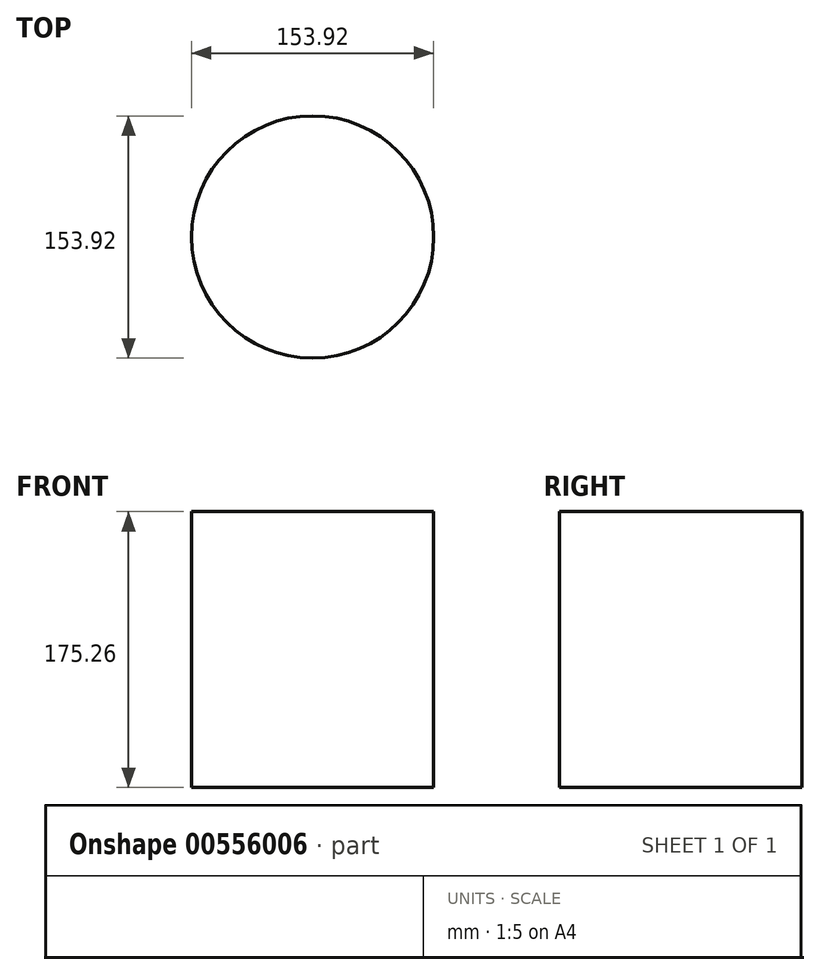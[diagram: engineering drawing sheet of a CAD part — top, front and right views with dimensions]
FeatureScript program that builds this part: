
annotation { "Feature Type Name" : "Feature", "Feature Type Description" : "" }
export const myFeature = defineFeature(function(context is Context, id is Id, definition is map)
    precondition{}
    {
        {
            var Q0;
            Q0=qCreatedBy(makeId("Top.planeOp"),FACE);
            var sketch = newSketch(context, id + "F0", { "sketchPlane" : qUnion([Q0])});
            skCircle(sketch, "E0", {"center": v(0, 0) * mm, "radius": 76.96 * mm});
            skSolve(sketch);
        }
        {
            var Q0;
            Q0=makeQuery(id+"F0.imprint","IMPRINT",FACE,{"disambiguationData":[TD([[makeQuery(id+"F0.imprint","IMPRINT",EDGE,{"derivedFrom":sQuery(id+"F0.wireOp",EDGE,"E0")}),1.0]])]});
            extrude(context, id + "F1", {"entities" : qUnion([Q0]), "depth" : 175.26 * mm, "offsetDistance" : 25.4 * mm});
        }
    });
